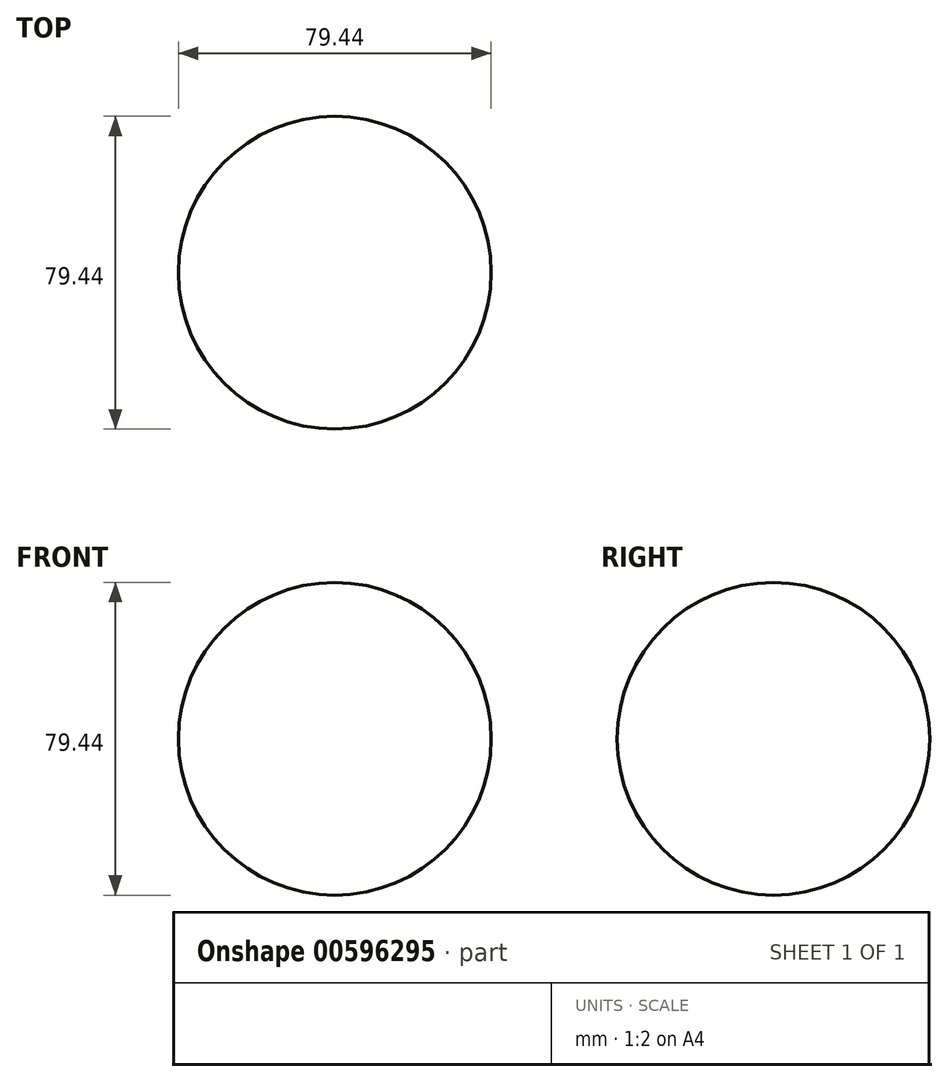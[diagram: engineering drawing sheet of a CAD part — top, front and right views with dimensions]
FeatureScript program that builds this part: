
annotation { "Feature Type Name" : "Feature", "Feature Type Description" : "" }
export const myFeature = defineFeature(function(context is Context, id is Id, definition is map)
    precondition{}
    {
        {
            var Q0;
            Q0=qCreatedBy(makeId("Front.planeOp"),FACE);
            var sketch = newSketch(context, id + "F0", { "sketchPlane" : qUnion([Q0])});
            skArc(sketch, "E0", {"start": v(0, 39.72) * mm, "mid": v(-39.72, 0) * mm, "end": v(0, -39.72) * mm});
            skLineSegment(sketch, "E1", {"start": v(0, -43.12) * mm, "end": v(0, 42.44) * mm});
            skSolve(sketch);
        }
        {
            var Q0;
            Q0=qCreatedBy(makeId("Front.planeOp"),FACE);
            var sketch = newSketch(context, id + "F1", { "sketchPlane" : qUnion([Q0])});
            skPoint(sketch, "E2.start.orphan", {"position": v(0, 36.55) * mm});
            skLineSegment(sketch, "E3", {"start": v(0, 36.55) * mm, "end": v(0, -37.22) * mm});
            skSolve(sketch);
        }
        {
            var Q0;
            {var subQ0=sQuery(id+"F0.wireOp",EDGE,"E0");Q0=makeQuery(id+"F0.imprint","IMPRINT",FACE,{"disambiguationData":[TD([[makeQuery(id+"F0.imprint","IMPRINT",EDGE,{"derivedFrom":subQ0}),1.0]])]});}
            var Q1;
            Q1=sQuery(id+"F1.wireOp",EDGE,"E3");
            revolve(context, id + "F2", {"entities" : qUnion([Q0]), "axis" : qUnion([Q1]), "revolveType" : RevolveType.FULL});
        }
    });
